# Revit family: Techlam Standard Post-180mm
name_source: partatom
category: Structural Columns
revit_build: Autodesk Revit 2016 (Build: 20150220_1215(x64)
units: mm (PartAtom-declared; Revit-internal decimal feet)

## family parameters
Always export as geometry = No
Beam cutback in plan = From bounding box
Cut with Voids When Loaded = No
Material for Model Behavior = Wood
Section Shape = Not Defined
Shared = No
Show family pre-cut in plan views = Yes

## types (21) — shared parameters
b = 180 mm  [stored 0.590551 ft]

## per-type parameters (varying)
| type | d |
| 88 x 180 | 88 mm  [stored 0.288714 ft] |
| 135 x 180 | 135 mm  [stored 0.442913 ft] |
| 140 x 180 | 140 mm  [stored 0.459318 ft] |
| 180 x 180 | 180 mm  [stored 0.590551 ft] |
| 190 x 180 | 190 mm |
| 225 x 180 | 225 mm  [stored 0.738189 ft] |
| 240 x 180 | 240 mm  [stored 0.787402 ft] |
| 270 x 180 | 270 mm  [stored 0.885827 ft] |
| 290 x 180 | 290 mm  [stored 0.951444 ft] |
| 315 x 180 | 315 mm  [stored 1.03346 ft] |
| 360 x 180 | 360 mm  [stored 1.1811 ft] |
| 405 x 180 | 405 mm |
| 450 x 180 | 450 mm  [stored 1.47638 ft] |
| 495 x 180 | 495 mm  [stored 1.62402 ft] |
| 540 x 180 | 540 mm  [stored 1.77165 ft] |
| 585 x 180 | 585 mm  [stored 1.91929 ft] |
| 630 x 180 | 630 mm  [stored 2.06693 ft] |
| 675 x 180 | 675 mm  [stored 2.21457 ft] |
| 720 x 180 | 720 mm  [stored 2.3622 ft] |
| 765 x 180 | 765 mm  [stored 2.50984 ft] |
| 810 x 180 | 810 mm |

note: [stored X ft] marks values corroborated as IEEE doubles in the binary element streams (Revit-internal decimal feet)

## geometry (parser evidence)
native form markers: Blend x4
no freeform markers — native parametric forms only
